# Revit family: smoothline_630x200_hl_led_19w_1460lm_3000k_cri80_410-1410
name_source: partatom
category: Leuchten
revit_build: Autodesk Revit 2016 (Build: 20190508_0715(x64)
units: mm (PartAtom-declared; Revit-internal decimal feet)

## family parameters
Basisbauteil = Fläche
Beim Laden mit Abzugskörper schneiden = Nein
Bemaßung runder Anschluss = Durchmesser verwenden
Gemeinsam genutzt = Nein
Lichtquelle = Nein
Raumberechnungspunkt = Nein
Teiletyp = Normal

## types (1)
- 410-1410-D01 (6 x LED, 429 lm, 3.2 W, 3000K)
    Approval mark = CE
    Beschreibung = The pendant luminaire SMOOTHLINE from the familiy SMOOTHY consists of aluminum-extruded profile. Charming SOFT-EDGE design ensure unparalleled styling. The ballast is integrated and allows for an operation with 220-240V (50/60Hz). SMOOTHLINE (# 410-1410) ist not dimmable (on/off). The luminaire with direct illumination and corresponds to protection class SK1 at IP20.
    CIE Flux Codes = 47 78 95 100 57
    Color Rendering = 1B/80…89
    Color Temperature = 3000K
    Height = 120 mm
    Hersteller = Prolicht
    Lamp Light Flux = 429 lm
    Lamp Power = 3.2 W
    Lamp count = 6
    Lampe = 6 x LED
    Length = 630 mm
    Luminous efficacy = 76 lm/W
    ModVariant = Nein
    Modell = 410-1410
    Mounting Place = Ceiling
    Mounting Type = Pendant
    Number of Poles = 1
    OnlyDefault = Ja
    Power Factor = 1
    Product Name = SMOOTHLINE 630x200 HL LED 19W 1460lm 3000K CRI80
    Product group = Suspended lights
    ProductGroupID = 941
    Protection Class = Protection class I
    Protection Degree = IP 20
    RLX_Detail_Level = 1
    RlxData = <blob elided: 47717 chars, md5=c5b43dab>
    Scheinlast = 19 VA
    Socket = socket
    Standby Power = 0 W
    System Light Flux = 1461 lm
    System Power = 19 W
    Typenbild = 410-1410.jpg
    URL = http://relux.com
    VarID = 410-1410-d01
    Voltage = 0 V
    Vorgabe-Ansicht = 1800 mm
    Weight = 0.00 kg
    Width = 200 mm  [stored 0.656168 ft]

note: [stored X ft] marks values corroborated as IEEE doubles in the binary element streams (Revit-internal decimal feet)

## geometry (parser evidence)
native form markers: Blend x4, Sweep x13
no freeform markers — native parametric forms only
